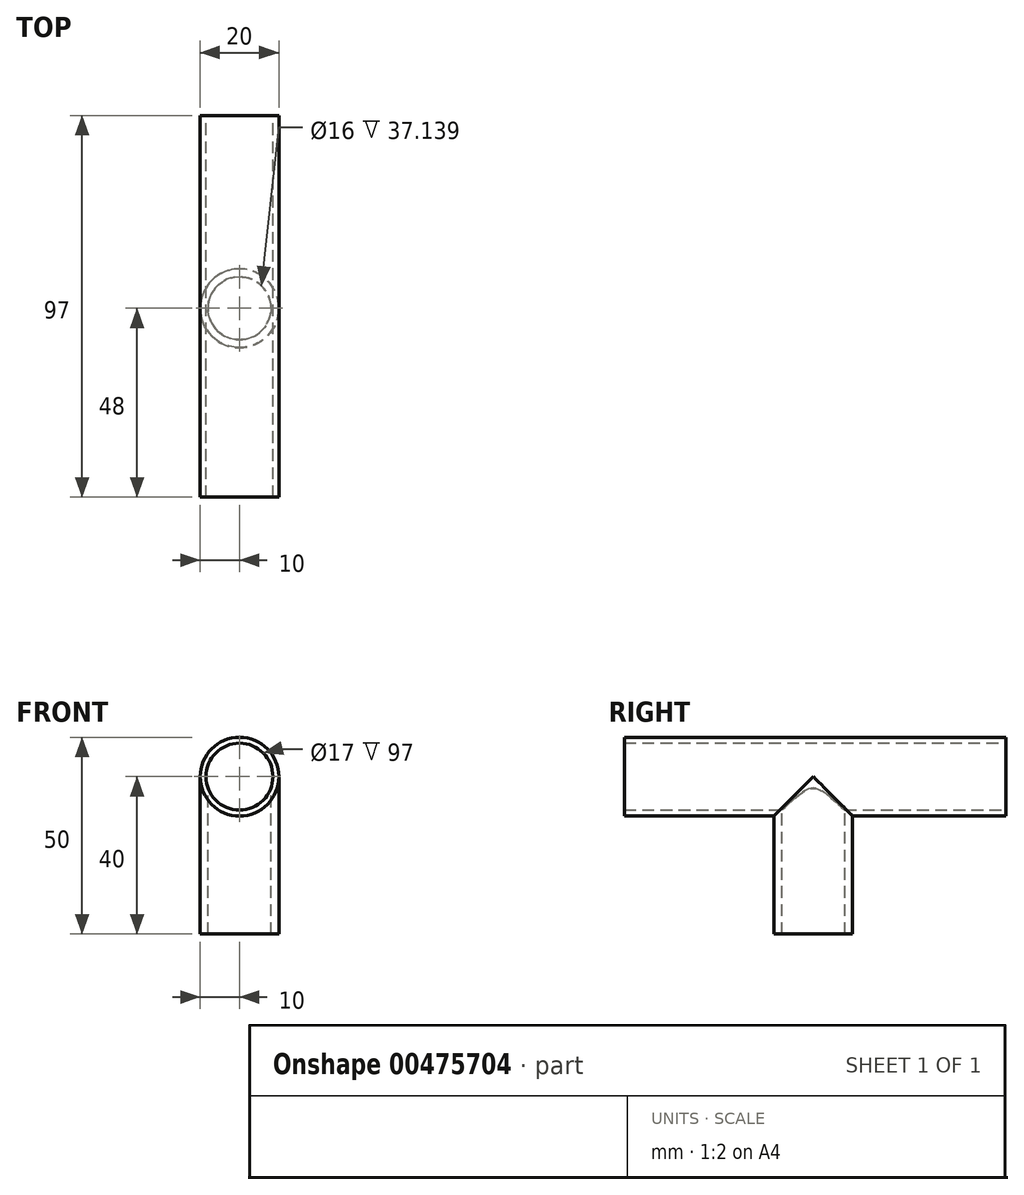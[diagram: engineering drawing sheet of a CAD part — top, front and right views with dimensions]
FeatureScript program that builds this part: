
annotation { "Feature Type Name" : "Feature", "Feature Type Description" : "" }
export const myFeature = defineFeature(function(context is Context, id is Id, definition is map)
    precondition{}
    {
        {
            var Q0;
            Q0=qCreatedBy(makeId("Front.planeOp"),FACE);
            var sketch = newSketch(context, id + "F0", { "sketchPlane" : qUnion([Q0])});
            skCircle(sketch, "E0", {"center": v(0, 0) * mm, "radius": 10 * mm});
            skCircle(sketch, "E1", {"center": v(0, 0) * mm, "radius": 8.5 * mm});
            skSolve(sketch);
        }
        {
            var Q0;
            Q0 = qSketchRegion(id + "F0", true);
            extrude(context, id + "F1", {"entities" : qUnion([Q0]), "depth" : 97 * mm, "offsetDistance" : 25 * mm});
        }
        {
            var Q0;
            Q0=qCreatedBy(makeId("Top.planeOp"),FACE);
            var sketch = newSketch(context, id + "F2", { "sketchPlane" : qUnion([Q0])});
            skLineSegment(sketch, "E2", {"start": v(0, 0) * mm, "end": v(0, -49) * mm, "construction": true});
            skCircle(sketch, "E3", {"center": v(0, -49) * mm, "radius": 10 * mm});
            skCircle(sketch, "E4", {"center": v(0, -49) * mm, "radius": 8 * mm});
            skSolve(sketch);
        }
        {
            var Q0;
            Q0 = qSketchRegion(id + "F2", true);
            extrude(context, id + "F3", {"entities" : qUnion([Q0]), "operationType" : NewBodyOperationType.ADD, "oppositeDirection" : true, "depth" : 40 * mm, "offsetDistance" : 25 * mm});
        }
        {
            var Q0;
            Q0=qCreatedBy(makeId("Top.planeOp"),FACE);
            var sketch = newSketch(context, id + "F4", { "sketchPlane" : qUnion([Q0])});
            skLineSegment(sketch, "E5", {"start": v(0, 0) * mm, "end": v(0, -49) * mm, "construction": true});
            skCircle(sketch, "E6", {"center": v(0, -49) * mm, "radius": 8 * mm});
            skSolve(sketch);
        }
        {
            var Q0;
            Q0 = qSketchRegion(id + "F4", true);
            extrude(context, id + "F5", {"entities" : qUnion([Q0]), "operationType" : NewBodyOperationType.REMOVE, "oppositeDirection" : true, "depth" : 59.3 * mm, "offsetDistance" : 25 * mm});
        }
        {
            var Q0;
            Q0=qCreatedBy(makeId("Front.planeOp"),FACE);
            var sketch = newSketch(context, id + "F6", { "sketchPlane" : qUnion([Q0])});
            skCircle(sketch, "E7", {"center": v(0, 0) * mm, "radius": 8.5 * mm});
            skSolve(sketch);
        }
        {
            var Q0;
            Q0 = qSketchRegion(id + "F6", true);
            extrude(context, id + "F7", {"entities" : qUnion([Q0]), "operationType" : NewBodyOperationType.REMOVE, "depth" : 110 * mm, "offsetDistance" : 25 * mm});
        }
    });
